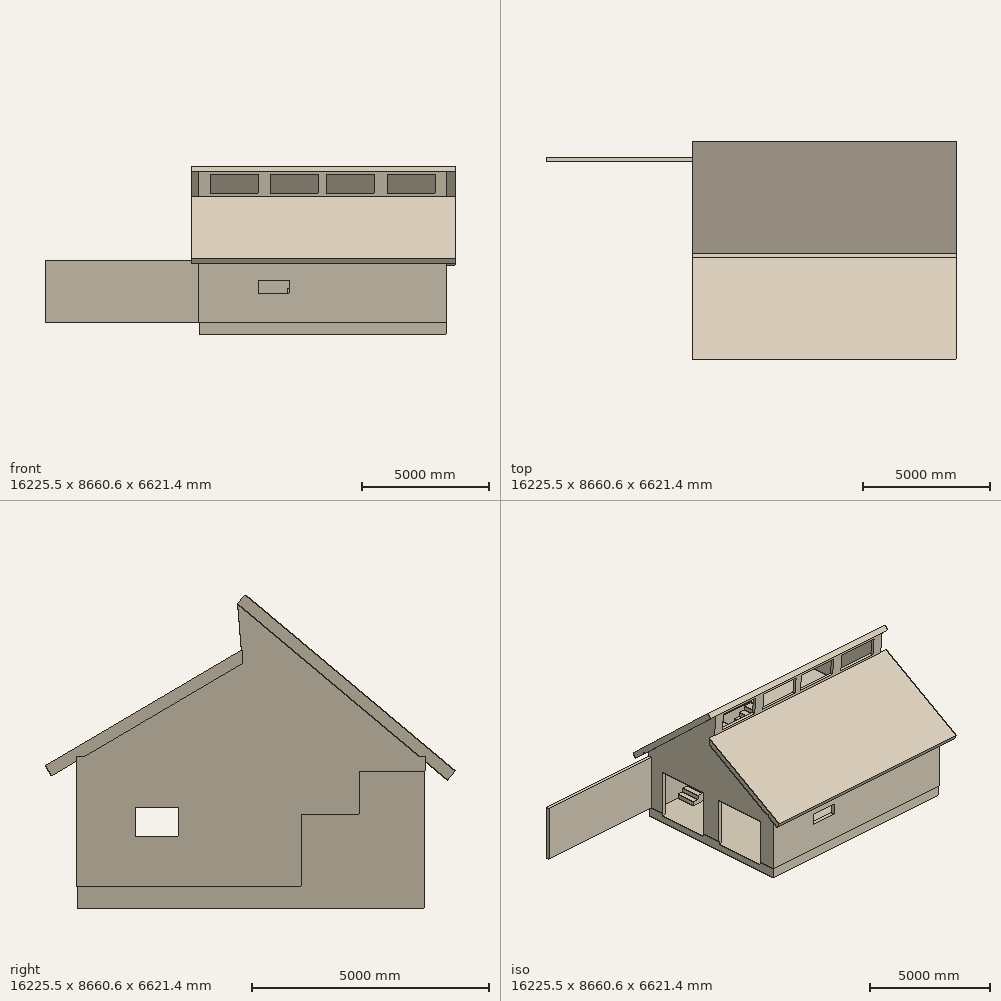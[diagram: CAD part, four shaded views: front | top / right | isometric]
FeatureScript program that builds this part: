
annotation { "Feature Type Name" : "Feature", "Feature Type Description" : "" }
export const myFeature = defineFeature(function(context is Context, id is Id, definition is map)
    precondition{}
    {
        {
            var Q0;
            Q0=qCreatedBy(makeId("Top.planeOp"),FACE);
            var sketch = newSketch(context, id + "F0", { "sketchPlane" : qUnion([Q0])});
            skLineSegment(sketch, "E0.bottom", {"start": v(0, 0) * mm, "end": v(9753.6, 0) * mm});
            skLineSegment(sketch, "E0.top", {"start": v(0, 7315.2) * mm, "end": v(9753.6, 7315.2) * mm});
            skLineSegment(sketch, "E0.left", {"start": v(0, 0) * mm, "end": v(0, 7315.2) * mm});
            skLineSegment(sketch, "E0.right", {"start": v(9753.6, 0) * mm, "end": v(9753.6, 7315.2) * mm});
            skSolve(sketch);
        }
        {
            var Q0;
            Q0=qSketchRegion(id+"F0",true);
            extrude(context, id + "F1", {"entities" : qUnion([Q0]), "depth" : 304.8 * mm});
        }
        {
            var Q0;
            Q0=makeQuery(id+"F1.opExtrude","CAP_FACE",FACE,{"disambiguationData":[OSD([sQuery(id+"F0.wireOp",EDGE,"E0.bottom"),sQuery(id+"F0.wireOp",EDGE,"E0.top"),sQuery(id+"F0.wireOp",EDGE,"E0.left"),sQuery(id+"F0.wireOp",EDGE,"E0.right")])],"isStart":false});
            var sketch = newSketch(context, id + "F2", { "sketchPlane" : qUnion([Q0])});
            skLineSegment(sketch, "E1", {"start": v(0, 0) * mm, "end": v(9753.6, 0) * mm});
            skLineSegment(sketch, "E2", {"start": v(9753.6, 0) * mm, "end": v(9753.6, 7315.2) * mm});
            skLineSegment(sketch, "E3", {"start": v(9753.6, 7315.2) * mm, "end": v(0, 7315.2) * mm});
            skLineSegment(sketch, "E4", {"start": v(152.4, 7162.8) * mm, "end": v(9601.2, 7162.8) * mm});
            skLineSegment(sketch, "E5", {"start": v(9601.2, 7162.8) * mm, "end": v(9601.2, 152.4) * mm});
            skLineSegment(sketch, "E6", {"start": v(9601.2, 152.4) * mm, "end": v(152.4, 152.4) * mm});
            skLineSegment(sketch, "E7", {"start": v(152.4, 152.4) * mm, "end": v(152.4, 762) * mm});
            skLineSegment(sketch, "E8", {"start": v(152.4, 762) * mm, "end": v(0, 762) * mm});
            skLineSegment(sketch, "E9", {"start": v(152.4, 3200.4) * mm, "end": v(0, 3200.4) * mm});
            skLineSegment(sketch, "E10.trimOffspring", {"start": v(0, 762) * mm, "end": v(0, 0) * mm});
            skLineSegment(sketch, "E11", {"start": v(0, 3200.4) * mm, "end": v(0, 4114.8) * mm});
            skLineSegment(sketch, "E12", {"start": v(0, 4114.8) * mm, "end": v(152.4, 4114.8) * mm});
            skLineSegment(sketch, "E13", {"start": v(152.4, 4114.8) * mm, "end": v(152.4, 3200.4) * mm});
            skLineSegment(sketch, "E14", {"start": v(152.4, 7162.8) * mm, "end": v(152.4, 6553.2) * mm});
            skLineSegment(sketch, "E15", {"start": v(152.4, 6553.2) * mm, "end": v(0, 6553.2) * mm});
            skLineSegment(sketch, "E16", {"start": v(0, 6553.2) * mm, "end": v(0, 7315.2) * mm});
            skSolve(sketch);
        }
        {
            var Q0;
            Q0=qSketchRegion(id+"F2",true);
            extrude(context, id + "F3", {"entities" : qUnion([Q0]), "operationType" : NewBodyOperationType.ADD, "depth" : 152.4 * mm});
        }
        {
            var Q0;
            Q0=makeQuery(id+"F3.opExtrude","CAP_FACE",FACE,{"disambiguationData":[OSD([sQuery(id+"F2.wireOp",EDGE,"E1"),sQuery(id+"F2.wireOp",EDGE,"E2"),sQuery(id+"F2.wireOp",EDGE,"E3"),sQuery(id+"F2.wireOp",EDGE,"CElO2aeV-4ry8-U5nN-VFw7-lKZjGSDdjc46"),sQuery(id+"F2.wireOp",EDGE,"aXI8KXb9-mfIK-bI9D-YpWg-9FVOQ1UAsdFk"),sQuery(id+"F2.wireOp",EDGE,"YwxrfCe7-5sPB-iO6G-MdUH-hFZLTdnCo4qc"),sQuery(id+"F2.wireOp",EDGE,"E4"),sQuery(id+"F2.wireOp",EDGE,"E5"),sQuery(id+"F2.wireOp",EDGE,"E6"),sQuery(id+"F2.wireOp",EDGE,"Ys2fWGzV-SD4m-ymG8-wGML-VrA4gOR2uk4F")])],"isStart":false});
            var sketch = newSketch(context, id + "F4", { "sketchPlane" : qUnion([Q0])});
            skLineSegment(sketch, "E17.3", {"start": v(-6096, 7162.8) * mm, "end": v(9601.2, 7162.8) * mm});
            skLineSegment(sketch, "E17.4", {"start": v(0, 7315.2) * mm, "end": v(9753.6, 7315.2) * mm});
            skLineSegment(sketch, "E18", {"start": v(9753.6, 7162.8) * mm, "end": v(9753.6, 7315.2) * mm});
            skLineSegment(sketch, "E19", {"start": v(9601.2, 7162.8) * mm, "end": v(9753.6, 7162.8) * mm});
            skLineSegment(sketch, "E20", {"start": v(0, 7315.2) * mm, "end": v(-6096, 7315.2) * mm});
            skLineSegment(sketch, "E21", {"start": v(-6096, 7315.2) * mm, "end": v(-6096, 7162.8) * mm});
            skSolve(sketch);
        }
        {
            var Q0;
            Q0=qSketchRegion(id+"F4",true);
            extrude(context, id + "F5", {"entities" : qUnion([Q0]), "operationType" : NewBodyOperationType.ADD, "depth" : 2438.4 * mm});
        }
        {
            var Q0;
            Q0=makeQuery(id+"F5.boolean.opBoolean","MERGE",FACE,{"derivedFrom":[makeQuery(id+"F3.boolean.opBoolean","MERGE",FACE,{"derivedFrom":[makeQuery(id+"F1.opExtrude","SWEPT_FACE",FACE,{"disambiguationData":[OSD([sQuery(id+"F0.wireOp",EDGE,"E0.right")])]}),makeQuery(id+"F3.opExtrude","SWEPT_FACE",FACE,{"disambiguationData":[OSD([sQuery(id+"F2.wireOp",EDGE,"E2")])]})]}),makeQuery(id+"F5.opExtrude","SWEPT_FACE",FACE,{"disambiguationData":[OSD([sQuery(id+"F4.wireOp",EDGE,"E18")])]})]});
            var sketch = newSketch(context, id + "F6", { "sketchPlane" : qUnion([Q0])});
            skLineSegment(sketch, "E22.0", {"start": v(4724.4, 457.2) * mm, "end": v(7162.8, 457.2) * mm});
            skLineSegment(sketch, "E22.1", {"start": v(7162.8, 2895.6) * mm, "end": v(7162.8, 457.2) * mm});
            skLineSegment(sketch, "E23", {"start": v(7162.8, 2895.6) * mm, "end": v(5943.6, 2895.6) * mm});
            skLineSegment(sketch, "E24", {"start": v(5943.6, 2895.6) * mm, "end": v(5943.6, 1981.2) * mm});
            skLineSegment(sketch, "E25", {"start": v(5943.6, 1981.2) * mm, "end": v(4724.4, 1981.2) * mm});
            skLineSegment(sketch, "E26", {"start": v(4724.4, 1981.2) * mm, "end": v(4724.4, 457.2) * mm});
            skPoint(sketch, "E27.orphan", {"position": v(0, 457.2) * mm});
            skSolve(sketch);
        }
        {
            var Q0;
            Q0=qSketchRegion(id+"F6",true);
            extrude(context, id + "F7", {"entities" : qUnion([Q0]), "operationType" : NewBodyOperationType.ADD, "oppositeDirection" : true, "depth" : 152.4 * mm});
        }
        {
            var Q0;
            Q0=makeQuery(id+"F5.boolean.opBoolean","MERGE",FACE,{"derivedFrom":[makeQuery(id+"F3.boolean.opBoolean","MERGE",FACE,{"derivedFrom":[makeQuery(id+"F1.opExtrude","SWEPT_FACE",FACE,{"disambiguationData":[OSD([sQuery(id+"F0.wireOp",EDGE,"E0.right")])]}),makeQuery(id+"F3.opExtrude","SWEPT_FACE",FACE,{"disambiguationData":[OSD([sQuery(id+"F2.wireOp",EDGE,"E2")])]})]}),makeQuery(id+"F5.opExtrude","SWEPT_FACE",FACE,{"disambiguationData":[OSD([sQuery(id+"F4.wireOp",EDGE,"E18")])]})]});
            var sketch = newSketch(context, id + "F8", { "sketchPlane" : qUnion([Q0])});
            skLineSegment(sketch, "E28.0", {"start": v(5943.6, 2895.6) * mm, "end": v(5943.6, 1981.2) * mm});
            skLineSegment(sketch, "E28.1", {"start": v(5943.6, 1981.2) * mm, "end": v(4724.4, 1981.2) * mm});
            skLineSegment(sketch, "E28.2", {"start": v(4724.4, 1981.2) * mm, "end": v(4724.4, 457.2) * mm});
            skLineSegment(sketch, "E28.3", {"start": v(0, 457.2) * mm, "end": v(4724.4, 457.2) * mm});
            skLineSegment(sketch, "E29", {"start": v(5943.6, 2895.6) * mm, "end": v(0, 2895.6) * mm});
            skLineSegment(sketch, "E30", {"start": v(0, 2895.6) * mm, "end": v(0, 457.2) * mm});
            skPoint(sketch, "E31.orphan", {"position": v(5943.6, 457.2) * mm});
            skLineSegment(sketch, "E32.bottom", {"start": v(1219.2, 2133.6) * mm, "end": v(2133.6, 2133.6) * mm});
            skLineSegment(sketch, "E32.top", {"start": v(1219.2, 1524) * mm, "end": v(2133.6, 1524) * mm});
            skLineSegment(sketch, "E32.left", {"start": v(1219.2, 2133.6) * mm, "end": v(1219.2, 1524) * mm});
            skLineSegment(sketch, "E32.right", {"start": v(2133.6, 2133.6) * mm, "end": v(2133.6, 1524) * mm});
            skSolve(sketch);
        }
        {
            var Q0;
            Q0=qSketchRegion(id+"F8",true);
            extrude(context, id + "F9", {"entities" : qUnion([Q0]), "oppositeDirection" : true, "depth" : 152.4 * mm, "hasSecondDirection" : true, "secondDirectionOppositeDirection" : false, "secondDirectionDepth" : 30.48 * mm});
        }
        {
            var Q0;
            Q0=makeQuery(id+"F3.boolean.opBoolean","MERGE",FACE,{"derivedFrom":[makeQuery(id+"F1.opExtrude","SWEPT_FACE",FACE,{"disambiguationData":[OSD([sQuery(id+"F0.wireOp",EDGE,"E0.bottom")])]}),makeQuery(id+"F3.opExtrude","SWEPT_FACE",FACE,{"disambiguationData":[OSD([sQuery(id+"F2.wireOp",EDGE,"UFMVc4qC-J9h5-cVFd-Tk5D-hxqTVF5q9AkB.bottom")])]}),makeQuery(id+"F3.opExtrude","SWEPT_FACE",FACE,{"disambiguationData":[OSD([sQuery(id+"F2.wireOp",EDGE,"E1")])]}),makeQuery(id+"F3.opExtrude","SWEPT_FACE",FACE,{"disambiguationData":[OSD([sQuery(id+"F2.wireOp",EDGE,"4jodHp1x-Gv9j-bjxU-Nll4-TZ1wEXyRSDHW")])]})]});
            var sketch = newSketch(context, id + "F10", { "sketchPlane" : qUnion([Q0])});
            skLineSegment(sketch, "E33.1", {"start": v(9784.08, 2895.6) * mm, "end": v(9784.08, 457.2) * mm});
            skLineSegment(sketch, "E34", {"start": v(-30.48, 457.2) * mm, "end": v(-30.48, 2895.6) * mm});
            skLineSegment(sketch, "E35.0", {"start": v(-30.48, 2895.6) * mm, "end": v(9601.2, 2895.6) * mm});
            skLineSegment(sketch, "E36", {"start": v(9601.2, 2895.6) * mm, "end": v(9784.08, 2895.6) * mm});
            skLineSegment(sketch, "E37", {"start": v(9784.08, 457.2) * mm, "end": v(-30.48, 457.2) * mm});
            skLineSegment(sketch, "E38.bottom", {"start": v(3559.92, 1627.82) * mm, "end": v(2338.45, 1627.82) * mm});
            skLineSegment(sketch, "E38.top", {"start": v(3559.92, 2112.53) * mm, "end": v(2338.45, 2112.53) * mm});
            skLineSegment(sketch, "E38.left", {"start": v(3559.92, 1627.82) * mm, "end": v(3559.92, 2112.53) * mm});
            skLineSegment(sketch, "E38.right", {"start": v(2338.45, 1627.82) * mm, "end": v(2338.45, 2112.53) * mm});
            skPoint(sketch, "E38.middle", {"position": v(2949.18, 1870.18) * mm});
            skLineSegment(sketch, "E39.0", {"start": v(0, 457.2) * mm, "end": v(9753.6, 457.2) * mm, "construction": true});
            skSolve(sketch);
        }
        {
            var Q0;
            Q0=qSketchRegion(id+"F10",true);
            extrude(context, id + "F11", {"entities" : qUnion([Q0]), "operationType" : NewBodyOperationType.ADD, "oppositeDirection" : true, "depth" : 152.4 * mm, "hasSecondDirection" : true, "secondDirectionOppositeDirection" : false, "secondDirectionDepth" : 30.48 * mm});
        }
        {
            var Q0;
            Q0=makeQuery(id+"F11.opExtrude","SWEPT_FACE",FACE,{"disambiguationData":[OSD([sQuery(id+"F10.wireOp",EDGE,"E34")])]});
            var sketch = newSketch(context, id + "F12", { "sketchPlane" : qUnion([Q0])});
            skLineSegment(sketch, "E40.0", {"start": v(0, 457.2) * mm, "end": v(-762, 457.2) * mm});
            skLineSegment(sketch, "E41.0", {"start": v(-3200.4, 457.2) * mm, "end": v(-4114.8, 457.2) * mm});
            skLineSegment(sketch, "E42.0", {"start": v(-6553.2, 457.2) * mm, "end": v(-7162.8, 457.2) * mm});
            skLineSegment(sketch, "E43", {"start": v(-762, 457.2) * mm, "end": v(-762, 2438.4) * mm});
            skLineSegment(sketch, "E44", {"start": v(-762, 2438.4) * mm, "end": v(-3200.4, 2438.4) * mm});
            skLineSegment(sketch, "E45", {"start": v(-3200.4, 2438.4) * mm, "end": v(-3200.4, 457.2) * mm});
            skLineSegment(sketch, "E46", {"start": v(-4114.8, 457.2) * mm, "end": v(-4114.8, 2438.4) * mm});
            skLineSegment(sketch, "E47", {"start": v(-4114.8, 2438.4) * mm, "end": v(-6553.2, 2438.4) * mm});
            skLineSegment(sketch, "E48", {"start": v(-6553.2, 2438.4) * mm, "end": v(-6553.2, 457.2) * mm});
            skLineSegment(sketch, "E49.0", {"start": v(30.48, 457.2) * mm, "end": v(30.48, 2895.6) * mm});
            skLineSegment(sketch, "E50", {"start": v(0, 457.2) * mm, "end": v(30.48, 457.2) * mm});
            skLineSegment(sketch, "E51.0", {"start": v(-7162.8, 2895.6) * mm, "end": v(-7162.8, 457.2) * mm});
            skLineSegment(sketch, "E52", {"start": v(-7162.8, 2895.6) * mm, "end": v(30.48, 2895.6) * mm});
            skPoint(sketch, "E53.orphan", {"position": v(-7162.8, 304.8) * mm});
            skSolve(sketch);
        }
        {
            var Q0;
            Q0=qSketchRegion(id+"F12",true);
            extrude(context, id + "F13", {"entities" : qUnion([Q0]), "operationType" : NewBodyOperationType.ADD, "oppositeDirection" : true, "depth" : 182.88 * mm});
        }
        {
            var Q0;
            Q0=makeQuery(id+"F13.boolean.opBoolean","MERGE",FACE,{"derivedFrom":[makeQuery(id+"F11.boolean.opBoolean","MERGE",FACE,{"derivedFrom":[makeQuery(id+"F9.opExtrude","SWEPT_FACE",FACE,{"disambiguationData":[OSD([sQuery(id+"F8.wireOp",EDGE,"E29")])]}),makeQuery(id+"F11.opExtrude","SWEPT_FACE",FACE,{"disambiguationData":[OSD([sQuery(id+"F10.wireOp",EDGE,"E35.0"),sQuery(id+"F10.wireOp",EDGE,"718a242f-b1c5-4c75-9c24-ae089a548528.0"),sQuery(id+"F10.wireOp",EDGE,"NqAyBP7R-1DhB-lObb-gTTq-B6LYnu6wACnz")])]})]}),makeQuery(id+"F13.opExtrude","SWEPT_FACE",FACE,{"disambiguationData":[OSD([sQuery(id+"F12.wireOp",EDGE,"rwMAnXGB-DcCB-V7dJ-406g-be1naIjNoRF5")])]})]});
            var sketch = newSketch(context, id + "F14", { "sketchPlane" : qUnion([Q0])});
            skLineSegment(sketch, "E54.bottom", {"start": v(9784.08, -30.48) * mm, "end": v(-30.48, -30.48) * mm});
            skLineSegment(sketch, "E54.top", {"start": v(9784.08, 7345.68) * mm, "end": v(-30.48, 7345.68) * mm});
            skLineSegment(sketch, "E54.left", {"start": v(9784.08, -30.48) * mm, "end": v(9784.08, 7345.68) * mm});
            skLineSegment(sketch, "E54.right", {"start": v(-30.48, -30.48) * mm, "end": v(-30.48, 7345.68) * mm});
            skLineSegment(sketch, "E55.0", {"start": v(152.4, 7162.8) * mm, "end": v(9601.2, 7162.8) * mm, "construction": true});
            skLineSegment(sketch, "E56.bottom", {"start": v(3810, 7162.8) * mm, "end": v(5842, 7162.8) * mm});
            skLineSegment(sketch, "E56.top", {"start": v(3810, 6248.4) * mm, "end": v(5842, 6248.4) * mm});
            skLineSegment(sketch, "E56.left", {"start": v(3810, 7162.8) * mm, "end": v(3810, 6248.4) * mm});
            skLineSegment(sketch, "E56.right", {"start": v(5842, 7162.8) * mm, "end": v(5842, 6248.4) * mm});
            skSolve(sketch);
        }
        {
            var Q0;
            Q0=qSketchRegion(id+"F14",true);
            extrude(context, id + "F15", {"entities" : qUnion([Q0]), "operationType" : NewBodyOperationType.ADD, "depth" : 304.8 * mm});
        }
        {
            var Q0;
            Q0=makeQuery(id+"F5.boolean.opBoolean","MERGE",FACE,{"derivedFrom":[makeQuery(id+"F3.opExtrude","SWEPT_FACE",FACE,{"disambiguationData":[OSD([sQuery(id+"F2.wireOp",EDGE,"E4")])]}),makeQuery(id+"F5.opExtrude","SWEPT_FACE",FACE,{"disambiguationData":[OSD([sQuery(id+"F4.wireOp",EDGE,"E17.3"),sQuery(id+"F4.wireOp",EDGE,"E19")])]})]});
            var sketch = newSketch(context, id + "F16", { "sketchPlane" : qUnion([Q0])});
            skLineSegment(sketch, "E57", {"start": v(1524, 304.8) * mm, "end": v(1524, 482.6) * mm});
            skLineSegment(sketch, "E58", {"start": v(1524, 482.6) * mm, "end": v(1803.4, 482.6) * mm});
            skLineSegment(sketch, "E59", {"start": v(1803.4, 482.6) * mm, "end": v(1803.4, 673.1) * mm});
            skLineSegment(sketch, "E60", {"start": v(1803.4, 673.1) * mm, "end": v(2082.8, 673.1) * mm});
            skLineSegment(sketch, "E61", {"start": v(2082.8, 673.1) * mm, "end": v(2082.8, 863.6) * mm});
            skLineSegment(sketch, "E62", {"start": v(2082.8, 863.6) * mm, "end": v(2362.2, 863.6) * mm});
            skLineSegment(sketch, "E63", {"start": v(2362.2, 863.6) * mm, "end": v(2362.2, 1054.1) * mm});
            skLineSegment(sketch, "E64", {"start": v(2362.2, 1054.1) * mm, "end": v(2641.6, 1054.1) * mm});
            skLineSegment(sketch, "E65", {"start": v(2641.6, 1054.1) * mm, "end": v(2641.6, 1244.6) * mm});
            skLineSegment(sketch, "E66", {"start": v(2641.6, 1244.6) * mm, "end": v(2921, 1244.6) * mm});
            skLineSegment(sketch, "E67", {"start": v(2921, 1244.6) * mm, "end": v(2921, 1435.1) * mm});
            skLineSegment(sketch, "E68", {"start": v(2921, 1435.1) * mm, "end": v(3200.4, 1435.1) * mm});
            skLineSegment(sketch, "E69", {"start": v(3200.4, 1435.1) * mm, "end": v(3200.4, 1625.6) * mm});
            skLineSegment(sketch, "E70", {"start": v(3200.4, 1625.6) * mm, "end": v(3479.8, 1625.6) * mm});
            skLineSegment(sketch, "E71", {"start": v(3479.8, 1625.6) * mm, "end": v(3479.8, 1816.1) * mm});
            skLineSegment(sketch, "E72", {"start": v(3479.8, 1816.1) * mm, "end": v(3759.2, 1816.1) * mm});
            skLineSegment(sketch, "E73", {"start": v(3759.2, 1816.1) * mm, "end": v(3759.2, 2006.6) * mm});
            skLineSegment(sketch, "E74", {"start": v(3759.2, 2006.6) * mm, "end": v(4038.6, 2006.6) * mm});
            skLineSegment(sketch, "E75", {"start": v(4038.6, 2006.6) * mm, "end": v(4038.6, 2197.1) * mm});
            skLineSegment(sketch, "E76", {"start": v(4038.6, 2197.1) * mm, "end": v(4318, 2197.1) * mm});
            skLineSegment(sketch, "E77", {"start": v(4318, 2197.1) * mm, "end": v(4318, 2387.6) * mm});
            skLineSegment(sketch, "E78", {"start": v(4318, 2387.6) * mm, "end": v(4597.4, 2387.6) * mm});
            skLineSegment(sketch, "E79", {"start": v(4597.4, 2387.6) * mm, "end": v(4597.4, 2578.1) * mm});
            skLineSegment(sketch, "E80", {"start": v(4597.4, 2578.1) * mm, "end": v(4876.8, 2578.1) * mm});
            skLineSegment(sketch, "E81", {"start": v(4876.8, 2578.1) * mm, "end": v(4876.8, 2768.6) * mm});
            skLineSegment(sketch, "E82", {"start": v(4876.8, 2768.6) * mm, "end": v(5156.2, 2768.6) * mm});
            skLineSegment(sketch, "E83", {"start": v(5156.2, 2768.6) * mm, "end": v(5156.2, 2959.1) * mm});
            skLineSegment(sketch, "E84", {"start": v(5156.2, 2959.1) * mm, "end": v(5435.6, 2959.1) * mm});
            skLineSegment(sketch, "E85", {"start": v(5435.6, 2959.1) * mm, "end": v(5435.6, 3149.6) * mm});
            skLineSegment(sketch, "E86", {"start": v(1524, 304.8) * mm, "end": v(2032, 304.8) * mm});
            skLineSegment(sketch, "E87", {"start": v(2032, 304.8) * mm, "end": v(5943.6, 3149.6) * mm});
            skLineSegment(sketch, "E88", {"start": v(5943.6, 3149.6) * mm, "end": v(5435.6, 3149.6) * mm});
            skSolve(sketch);
        }
        {
            var Q0;
            Q0=qSketchRegion(id+"F16",true);
            extrude(context, id + "F17", {"entities" : qUnion([Q0]), "depth" : 914.4 * mm});
        }
        {
            var Q0;
            Q0=makeQuery(id+"F15.boolean.opBoolean","MERGE",FACE,{"derivedFrom":[makeQuery(id+"F13.boolean.opBoolean","MERGE",FACE,{"derivedFrom":[makeQuery(id+"F11.opExtrude","SWEPT_FACE",FACE,{"disambiguationData":[OSD([sQuery(id+"F10.wireOp",EDGE,"E34")])]}),makeQuery(id+"F13.opExtrude","CAP_FACE",FACE,{"disambiguationData":[OSD([sQuery(id+"F12.wireOp",EDGE,"e79305b5-6bfb-4aba-b3ad-f4f6c9165815.0"),sQuery(id+"F12.wireOp",EDGE,"e79305b5-6bfb-4aba-b3ad-f4f6c9165815.1"),sQuery(id+"F12.wireOp",EDGE,"e79305b5-6bfb-4aba-b3ad-f4f6c9165815.2"),sQuery(id+"F12.wireOp",EDGE,"e79305b5-6bfb-4aba-b3ad-f4f6c9165815.3"),sQuery(id+"F12.wireOp",EDGE,"e79305b5-6bfb-4aba-b3ad-f4f6c9165815.4"),sQuery(id+"F12.wireOp",EDGE,"rwMAnXGB-DcCB-V7dJ-406g-be1naIjNoRF5"),sQuery(id+"F12.wireOp",EDGE,"RV3dmTTu-X8Ea-Aqf8-QfJf-1CL7oE8ZFLIE.bottom"),sQuery(id+"F12.wireOp",EDGE,"RV3dmTTu-X8Ea-Aqf8-QfJf-1CL7oE8ZFLIE.top"),sQuery(id+"F12.wireOp",EDGE,"RV3dmTTu-X8Ea-Aqf8-QfJf-1CL7oE8ZFLIE.left"),sQuery(id+"F12.wireOp",EDGE,"RV3dmTTu-X8Ea-Aqf8-QfJf-1CL7oE8ZFLIE.right"),sQuery(id+"F12.wireOp",EDGE,"iVETkI1e-IECp-0zC1-p8Mt-FjZXSi4iMt0L"),sQuery(id+"F12.wireOp",EDGE,"YfylPYB8-QBd5-X29u-F0Dp-1gZUZ0fhnGDs"),sQuery(id+"F12.wireOp",EDGE,"RpszpKaN-BTnz-HRhg-PGmq-AOTSQibeJWVN"),sQuery(id+"F12.wireOp",EDGE,"z04fkN9I-LUD8-M2hR-9kCB-Sq6xIk27uI4W")])],"isStart":true})]}),makeQuery(id+"F15.opExtrude","SWEPT_FACE",FACE,{"disambiguationData":[OSD([sQuery(id+"F14.wireOp",EDGE,"E54.right")])]})]});
            var sketch = newSketch(context, id + "F18", { "sketchPlane" : qUnion([Q0])});
            skLineSegment(sketch, "E89", {"start": v(-7812.66, 2701.02) * mm, "end": v(-7345.68, 3092.87) * mm});
            skLineSegment(sketch, "E90", {"start": v(-7345.68, 3092.87) * mm, "end": v(-7345.68, 3200.4) * mm});
            skLineSegment(sketch, "E91", {"start": v(-7345.68, 3200.4) * mm, "end": v(-7217.53, 3200.4) * mm});
            skLineSegment(sketch, "E92", {"start": v(-7217.53, 3200.4) * mm, "end": v(-3372.41, 6426.84) * mm});
            skLineSegment(sketch, "E93", {"start": v(-3372.41, 6426.84) * mm, "end": v(-3535.68, 6621.41) * mm});
            skLineSegment(sketch, "E94", {"start": v(-3535.68, 6621.41) * mm, "end": v(-7975.93, 2895.6) * mm});
            skLineSegment(sketch, "E95", {"start": v(-7975.93, 2895.6) * mm, "end": v(-7812.66, 2701.02) * mm});
            skLineSegment(sketch, "E96", {"start": v(-3473.58, 5457.64) * mm, "end": v(684.64, 3008.26) * mm});
            skLineSegment(sketch, "E97", {"start": v(684.64, 3008.26) * mm, "end": v(555.73, 2789.4) * mm});
            skLineSegment(sketch, "E98", {"start": v(555.73, 2789.4) * mm, "end": v(30.48, 3098.8) * mm});
            skLineSegment(sketch, "E99", {"start": v(30.48, 3098.8) * mm, "end": v(30.48, 3200.4) * mm});
            skLineSegment(sketch, "E100", {"start": v(30.48, 3200.4) * mm, "end": v(-142, 3200.4) * mm});
            skLineSegment(sketch, "E101", {"start": v(-142, 3200.4) * mm, "end": v(-3473.58, 5162.85) * mm});
            skLineSegment(sketch, "E102", {"start": v(-3473.58, 5457.64) * mm, "end": v(-3473.58, 5162.85) * mm});
            skPoint(sketch, "E103.orphan", {"position": v(-4299.2, 5649.17) * mm});
            skPoint(sketch, "E104.start.orphan", {"position": v(-3839.4, 6035) * mm});
            skSolve(sketch);
        }
        {
            var Q0;
            Q0=qSketchRegion(id+"F18",true);
            extrude(context, id + "F19", {"entities" : qUnion([Q0]), "operationType" : NewBodyOperationType.ADD, "depth" : 304.8 * mm, "hasSecondDirection" : true, "secondDirectionOppositeDirection" : true, "secondDirectionDepth" : 10160 * mm});
        }
        {
            var Q0;
            Q0=makeQuery(id+"F15.boolean.opBoolean","MERGE",FACE,{"derivedFrom":[makeQuery(id+"F13.boolean.opBoolean","MERGE",FACE,{"derivedFrom":[makeQuery(id+"F11.opExtrude","SWEPT_FACE",FACE,{"disambiguationData":[OSD([sQuery(id+"F10.wireOp",EDGE,"E34")])]}),makeQuery(id+"F13.opExtrude","CAP_FACE",FACE,{"disambiguationData":[OSD([sQuery(id+"F12.wireOp",EDGE,"e79305b5-6bfb-4aba-b3ad-f4f6c9165815.0"),sQuery(id+"F12.wireOp",EDGE,"e79305b5-6bfb-4aba-b3ad-f4f6c9165815.1"),sQuery(id+"F12.wireOp",EDGE,"e79305b5-6bfb-4aba-b3ad-f4f6c9165815.2"),sQuery(id+"F12.wireOp",EDGE,"e79305b5-6bfb-4aba-b3ad-f4f6c9165815.3"),sQuery(id+"F12.wireOp",EDGE,"e79305b5-6bfb-4aba-b3ad-f4f6c9165815.4"),sQuery(id+"F12.wireOp",EDGE,"rwMAnXGB-DcCB-V7dJ-406g-be1naIjNoRF5"),sQuery(id+"F12.wireOp",EDGE,"RV3dmTTu-X8Ea-Aqf8-QfJf-1CL7oE8ZFLIE.bottom"),sQuery(id+"F12.wireOp",EDGE,"RV3dmTTu-X8Ea-Aqf8-QfJf-1CL7oE8ZFLIE.top"),sQuery(id+"F12.wireOp",EDGE,"RV3dmTTu-X8Ea-Aqf8-QfJf-1CL7oE8ZFLIE.left"),sQuery(id+"F12.wireOp",EDGE,"RV3dmTTu-X8Ea-Aqf8-QfJf-1CL7oE8ZFLIE.right"),sQuery(id+"F12.wireOp",EDGE,"iVETkI1e-IECp-0zC1-p8Mt-FjZXSi4iMt0L"),sQuery(id+"F12.wireOp",EDGE,"YfylPYB8-QBd5-X29u-F0Dp-1gZUZ0fhnGDs"),sQuery(id+"F12.wireOp",EDGE,"RpszpKaN-BTnz-HRhg-PGmq-AOTSQibeJWVN"),sQuery(id+"F12.wireOp",EDGE,"z04fkN9I-LUD8-M2hR-9kCB-Sq6xIk27uI4W")])],"isStart":true})]}),makeQuery(id+"F15.opExtrude","SWEPT_FACE",FACE,{"disambiguationData":[OSD([sQuery(id+"F14.wireOp",EDGE,"E54.right")])]})]});
            var sketch = newSketch(context, id + "F20", { "sketchPlane" : qUnion([Q0])});
            skLineSegment(sketch, "E105.0", {"start": v(-7217.53, 3200.4) * mm, "end": v(-142, 3200.4) * mm});
            skLineSegment(sketch, "E106.0", {"start": v(-7217.53, 3200.4) * mm, "end": v(-3372.41, 6426.84) * mm});
            skLineSegment(sketch, "E107.0", {"start": v(-142, 3200.4) * mm, "end": v(-3473.58, 5162.85) * mm});
            skLineSegment(sketch, "E108", {"start": v(-3372.41, 6426.84) * mm, "end": v(-3473.58, 5162.85) * mm});
            skSolve(sketch);
        }
        {
            var Q0;
            Q0=qSketchRegion(id+"F20",true);
            extrude(context, id + "F21", {"entities" : qUnion([Q0]), "operationType" : NewBodyOperationType.ADD, "oppositeDirection" : true, "depth" : 152.4 * mm});
        }
        {
            var Q0;
            Q0=makeQuery(id+"F15.boolean.opBoolean","MERGE",FACE,{"derivedFrom":[makeQuery(id+"F11.boolean.opBoolean","MERGE",FACE,{"derivedFrom":[makeQuery(id+"F9.opExtrude","CAP_FACE",FACE,{"disambiguationData":[OSD([sQuery(id+"F8.wireOp",EDGE,"E28.0"),sQuery(id+"F8.wireOp",EDGE,"E28.1"),sQuery(id+"F8.wireOp",EDGE,"E28.2"),sQuery(id+"F8.wireOp",EDGE,"E28.3"),sQuery(id+"F8.wireOp",EDGE,"E29"),sQuery(id+"F8.wireOp",EDGE,"E30"),sQuery(id+"F8.wireOp",EDGE,"E32.bottom"),sQuery(id+"F8.wireOp",EDGE,"E32.top"),sQuery(id+"F8.wireOp",EDGE,"E32.left"),sQuery(id+"F8.wireOp",EDGE,"E32.right")])],"isStart":true}),makeQuery(id+"F11.opExtrude","SWEPT_FACE",FACE,{"disambiguationData":[OSD([sQuery(id+"F10.wireOp",EDGE,"E33.1")])]})]}),makeQuery(id+"F15.opExtrude","SWEPT_FACE",FACE,{"disambiguationData":[OSD([sQuery(id+"F14.wireOp",EDGE,"E54.left")])]})]});
            var sketch = newSketch(context, id + "F22", { "sketchPlane" : qUnion([Q0])});
            skLineSegment(sketch, "E109.0", {"start": v(7217.53, 3200.4) * mm, "end": v(142, 3200.4) * mm});
            skLineSegment(sketch, "E110.0", {"start": v(7217.53, 3200.4) * mm, "end": v(3372.41, 6426.84) * mm});
            skLineSegment(sketch, "E111.0", {"start": v(142, 3200.4) * mm, "end": v(3473.58, 5162.85) * mm});
            skLineSegment(sketch, "E112", {"start": v(3372.41, 6426.84) * mm, "end": v(3473.58, 5162.85) * mm});
            skSolve(sketch);
        }
        {
            var Q0;
            Q0=qSketchRegion(id+"F22",true);
            extrude(context, id + "F23", {"entities" : qUnion([Q0]), "operationType" : NewBodyOperationType.ADD, "oppositeDirection" : true, "depth" : 152.4 * mm});
        }
        {
            var Q0;
            Q0=makeQuery(id+"F21.opExtrude","SWEPT_FACE",FACE,{"disambiguationData":[OSD([sQuery(id+"F20.wireOp",EDGE,"E108")])]});
            var sketch = newSketch(context, id + "F24", { "sketchPlane" : qUnion([Q0])});
            skLineSegment(sketch, "E113.0", {"start": v(9784.08, 6137.29) * mm, "end": v(9784.08, 5151.68) * mm});
            skLineSegment(sketch, "E114.0", {"start": v(-30.48, 6137.29) * mm, "end": v(-30.48, 5151.68) * mm});
            skLineSegment(sketch, "E115", {"start": v(-30.48, 6137.29) * mm, "end": v(9784.08, 6137.29) * mm});
            skLineSegment(sketch, "E116", {"start": v(9784.08, 5151.68) * mm, "end": v(-30.48, 5151.68) * mm});
            skLineSegment(sketch, "E117", {"start": v(4876.8, 5151.68) * mm, "end": v(4876.8, 7522.2) * mm, "construction": true});
            skPoint(sketch, "E117.endSnap0", {"position": v(4876.8, 6137.29) * mm});
            skLineSegment(sketch, "E118", {"start": v(-1301.1, 8944.92) * mm, "end": v(0, 8944.92) * mm});
            skLineSegment(sketch, "E119.bottom", {"start": v(426.72, 5266.38) * mm, "end": v(2331.72, 5266.38) * mm});
            skLineSegment(sketch, "E119.top", {"start": v(426.72, 6028.38) * mm, "end": v(2331.72, 6028.38) * mm});
            skLineSegment(sketch, "E119.left", {"start": v(426.72, 5266.38) * mm, "end": v(426.72, 6028.38) * mm});
            skLineSegment(sketch, "E119.right", {"start": v(2331.72, 5266.38) * mm, "end": v(2331.72, 6028.38) * mm});
            skLineSegment(sketch, "E120.bottom", {"start": v(2814.32, 6028.38) * mm, "end": v(4719.32, 6028.38) * mm});
            skLineSegment(sketch, "E120.top", {"start": v(2814.32, 5279.2) * mm, "end": v(4719.32, 5279.2) * mm});
            skLineSegment(sketch, "E120.left", {"start": v(2814.32, 6028.38) * mm, "end": v(2814.32, 5279.2) * mm});
            skLineSegment(sketch, "E120.right", {"start": v(4719.32, 6028.38) * mm, "end": v(4719.32, 5279.2) * mm});
            skLineSegment(sketch, "E121.MirrorCS", {"start": v(7421.88, 5266.38) * mm, "end": v(7421.88, 6028.38) * mm});
            skLineSegment(sketch, "E122.MirrorCS", {"start": v(9326.88, 5266.38) * mm, "end": v(9326.88, 6028.38) * mm});
            skLineSegment(sketch, "E123.MirrorCS", {"start": v(9326.88, 6028.38) * mm, "end": v(7421.88, 6028.38) * mm});
            skLineSegment(sketch, "E124.MirrorCS", {"start": v(9326.88, 5266.38) * mm, "end": v(7421.88, 5266.38) * mm});
            skLineSegment(sketch, "E125.MirrorCS", {"start": v(6939.28, 6028.38) * mm, "end": v(5034.28, 6028.38) * mm});
            skLineSegment(sketch, "E126.MirrorCS", {"start": v(6939.28, 5279.2) * mm, "end": v(5034.28, 5279.2) * mm});
            skLineSegment(sketch, "E127.MirrorCS", {"start": v(6939.28, 6028.38) * mm, "end": v(6939.28, 5279.2) * mm});
            skLineSegment(sketch, "E128.MirrorCS", {"start": v(5034.28, 6028.38) * mm, "end": v(5034.28, 5279.2) * mm});
            skLineSegment(sketch, "E129.MirrorCS", {"start": v(-30.48, 5151.68) * mm, "end": v(9784.08, 5151.68) * mm});
            skSolve(sketch);
        }
        {
            var Q0;
            Q0=qSketchRegion(id+"F24",true);
            extrude(context, id + "F25", {"entities" : qUnion([Q0]), "operationType" : NewBodyOperationType.ADD, "oppositeDirection" : true, "depth" : 127 * mm});
        }
    });
